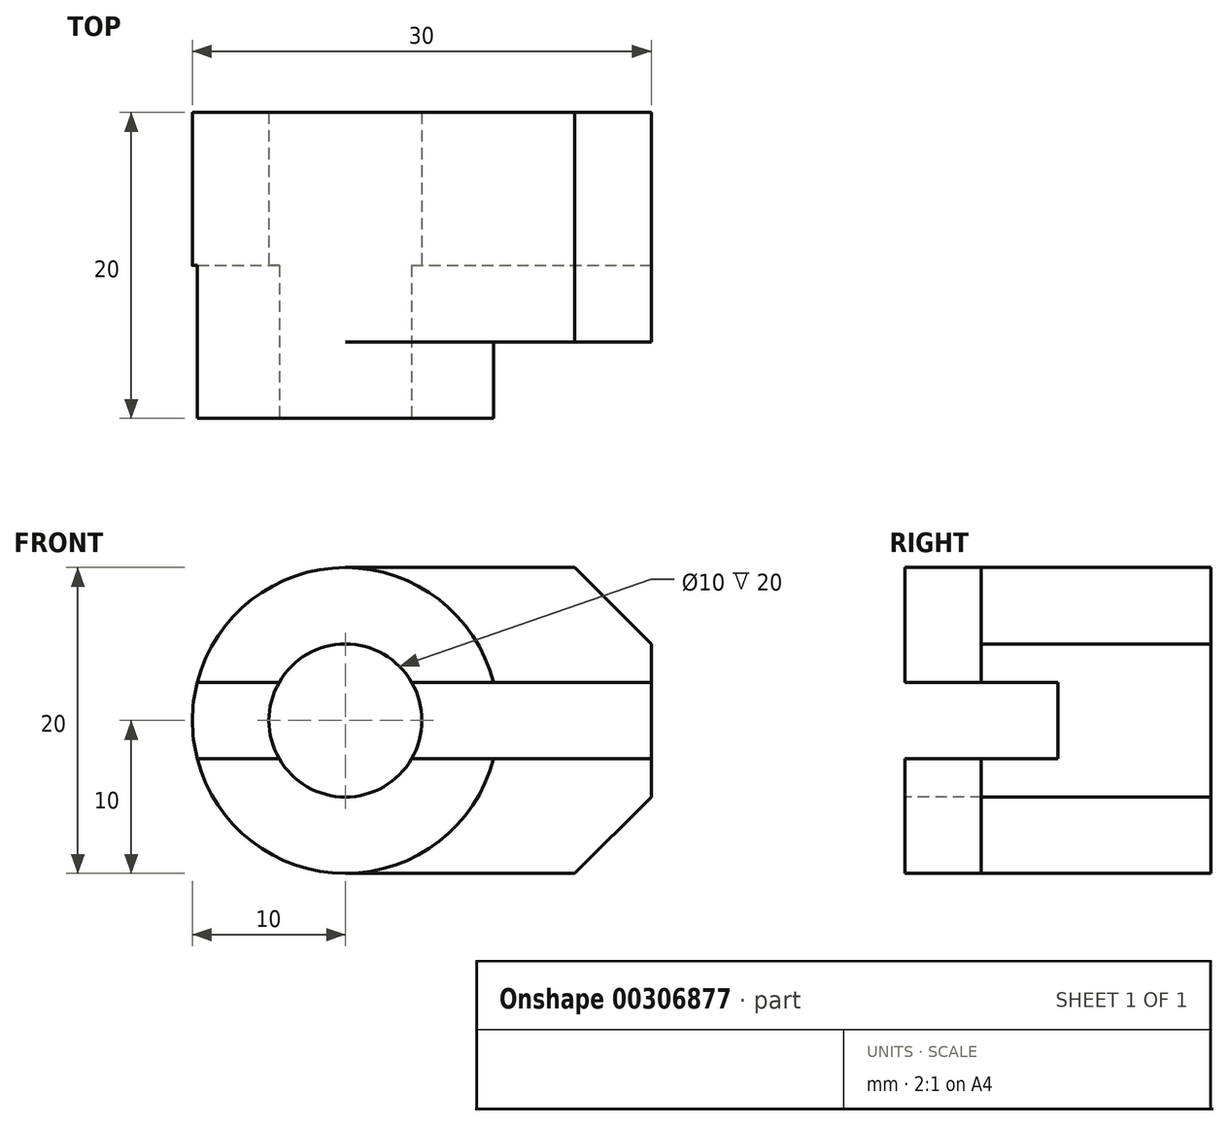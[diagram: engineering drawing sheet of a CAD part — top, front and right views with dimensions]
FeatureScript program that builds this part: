
annotation { "Feature Type Name" : "Feature", "Feature Type Description" : "" }
export const myFeature = defineFeature(function(context is Context, id is Id, definition is map)
    precondition{}
    {
        {
            var Q0;
            Q0=qCreatedBy(makeId("Front.planeOp"),FACE);
            var sketch = newSketch(context, id + "F0", { "sketchPlane" : qUnion([Q0])});
            skCircle(sketch, "E0", {"center": v(0, 0) * mm, "radius": 10 * mm});
            skLineSegment(sketch, "E1", {"start": v(0, 10) * mm, "end": v(15, 10) * mm});
            skLineSegment(sketch, "E2", {"start": v(15, 10) * mm, "end": v(20, 5) * mm});
            skLineSegment(sketch, "E3", {"start": v(20, 5) * mm, "end": v(20, -5) * mm});
            skLineSegment(sketch, "E4", {"start": v(20, -5) * mm, "end": v(15, -10) * mm});
            skLineSegment(sketch, "E5", {"start": v(15, -10) * mm, "end": v(0, -10) * mm});
            skSolve(sketch);
        }
        {
            var Q0;
            {var subQ0=sQuery(id+"F0.wireOp",EDGE,"E0");var subQ1=makeQuery(id+"F0.imprint","INTERSECT",VERTEX,{"derivedFrom":[subQ0,sQuery(id+"F0.wireOp",EDGE,"E1")]});Q0=makeQuery(id+"F0.imprint","IMPRINT",FACE,{"disambiguationData":[TD([[makeQuery(id+"F0.imprint","IMPRINT",EDGE,{"disambiguationData":[TD([[subQ1,-1.0]])],"derivedFrom":subQ0}),1.0]])]});}
            extrude(context, id + "F1", {"entities" : qUnion([Q0]), "depth" : 5 * mm});
        }
        {
            var Q0;
            {var subQ0=sQuery(id+"F0.wireOp",EDGE,"E0");var subQ1=makeQuery(id+"F0.imprint","INTERSECT",VERTEX,{"derivedFrom":[subQ0,sQuery(id+"F0.wireOp",EDGE,"E1")]});Q0=makeQuery(id+"F0.imprint","IMPRINT",FACE,{"disambiguationData":[TD([[makeQuery(id+"F0.imprint","IMPRINT",EDGE,{"disambiguationData":[TD([[subQ1,-1.0]])],"derivedFrom":subQ0}),1.0]])]});}
            var Q1;
            {var subQ0=sQuery(id+"F0.wireOp",EDGE,"E1");Q1=makeQuery(id+"F0.imprint","IMPRINT",FACE,{"disambiguationData":[TD([[makeQuery(id+"F0.imprint","IMPRINT",EDGE,{"derivedFrom":subQ0}),-1.0]])]});}
            extrude(context, id + "F2", {"entities" : qUnion([Q0, Q1]), "operationType" : NewBodyOperationType.ADD, "oppositeDirection" : true, "depth" : 15 * mm});
        }
        {
            var Q0;
            Q0=makeQuery(id+"F2.opExtrude","SWEPT_FACE",FACE,{"disambiguationData":[OSD([sQuery(id+"F0.wireOp",EDGE,"E3")])]});
            var sketch = newSketch(context, id + "F3", { "sketchPlane" : qUnion([Q0])});
            skLineSegment(sketch, "E6.bottom", {"start": v(-5, 2.5) * mm, "end": v(5, 2.5) * mm});
            skLineSegment(sketch, "E6.top", {"start": v(-5, -2.5) * mm, "end": v(5, -2.5) * mm});
            skLineSegment(sketch, "E6.left", {"start": v(-5, 2.5) * mm, "end": v(-5, -2.5) * mm});
            skLineSegment(sketch, "E6.right", {"start": v(5, 2.5) * mm, "end": v(5, -2.5) * mm});
            skLineSegment(sketch, "E7", {"start": v(0, 0) * mm, "end": v(5, 0) * mm, "construction": true});
            skSolve(sketch);
        }
        {
            var Q0;
            {var subQ0=sQuery(id+"F3.wireOp",EDGE,"E6.right");Q0=makeQuery(id+"F3.imprint","IMPRINT",FACE,{"disambiguationData":[TD([[makeQuery(id+"F3.imprint","IMPRINT",EDGE,{"derivedFrom":subQ0}),-1.0]])]});}
            var Q1;
            {var subQ0=sQuery(id+"F3.wireOp",EDGE,"E6.left");Q1=makeQuery(id+"F3.imprint","IMPRINT",FACE,{"disambiguationData":[TD([[makeQuery(id+"F3.imprint","IMPRINT",EDGE,{"derivedFrom":subQ0}),1.0]])]});}
            extrude(context, id + "F4", {"entities" : qUnion([Q0, Q1]), "operationType" : NewBodyOperationType.REMOVE, "endBound" : BoundingType.THROUGH_ALL, "oppositeDirection" : true, "depth" : 25 * mm});
        }
        {
            var Q0;
            {var subQ0=sQuery(id+"F0.wireOp",EDGE,"E0");var subQ1=makeQuery(id+"F0.imprint","INTERSECT",VERTEX,{"derivedFrom":[subQ0,sQuery(id+"F0.wireOp",EDGE,"E1")]});Q0=makeQuery(id+"F0.imprint","IMPRINT",FACE,{"disambiguationData":[TD([[makeQuery(id+"F0.imprint","IMPRINT",EDGE,{"disambiguationData":[TD([[subQ1,-1.0]])],"derivedFrom":subQ0}),1.0]])]});}
            var sketch = newSketch(context, id + "F5", { "sketchPlane" : qUnion([Q0])});
            skCircle(sketch, "E8", {"center": v(0, 0) * mm, "radius": 5 * mm});
            skSolve(sketch);
        }
        {
            var Q0;
            Q0 = qSketchRegion(id + "F5", true);
            var Q1;
            Q1=sQuery(id+"F5.wireOp",EDGE,"E8");
            extrude(context, id + "F6", {"entities" : qUnion([Q0]), "operationType" : NewBodyOperationType.REMOVE, "surfaceEntities" : qUnion([Q1]), "endBound" : BoundingType.THROUGH_ALL, "oppositeDirection" : true, "depth" : 25 * mm, "hasSecondDirection" : true, "secondDirectionBound" : BoundingType.THROUGH_ALL, "secondDirectionOppositeDirection" : false, "secondDirectionDepth" : 25 * mm});
        }
    });
